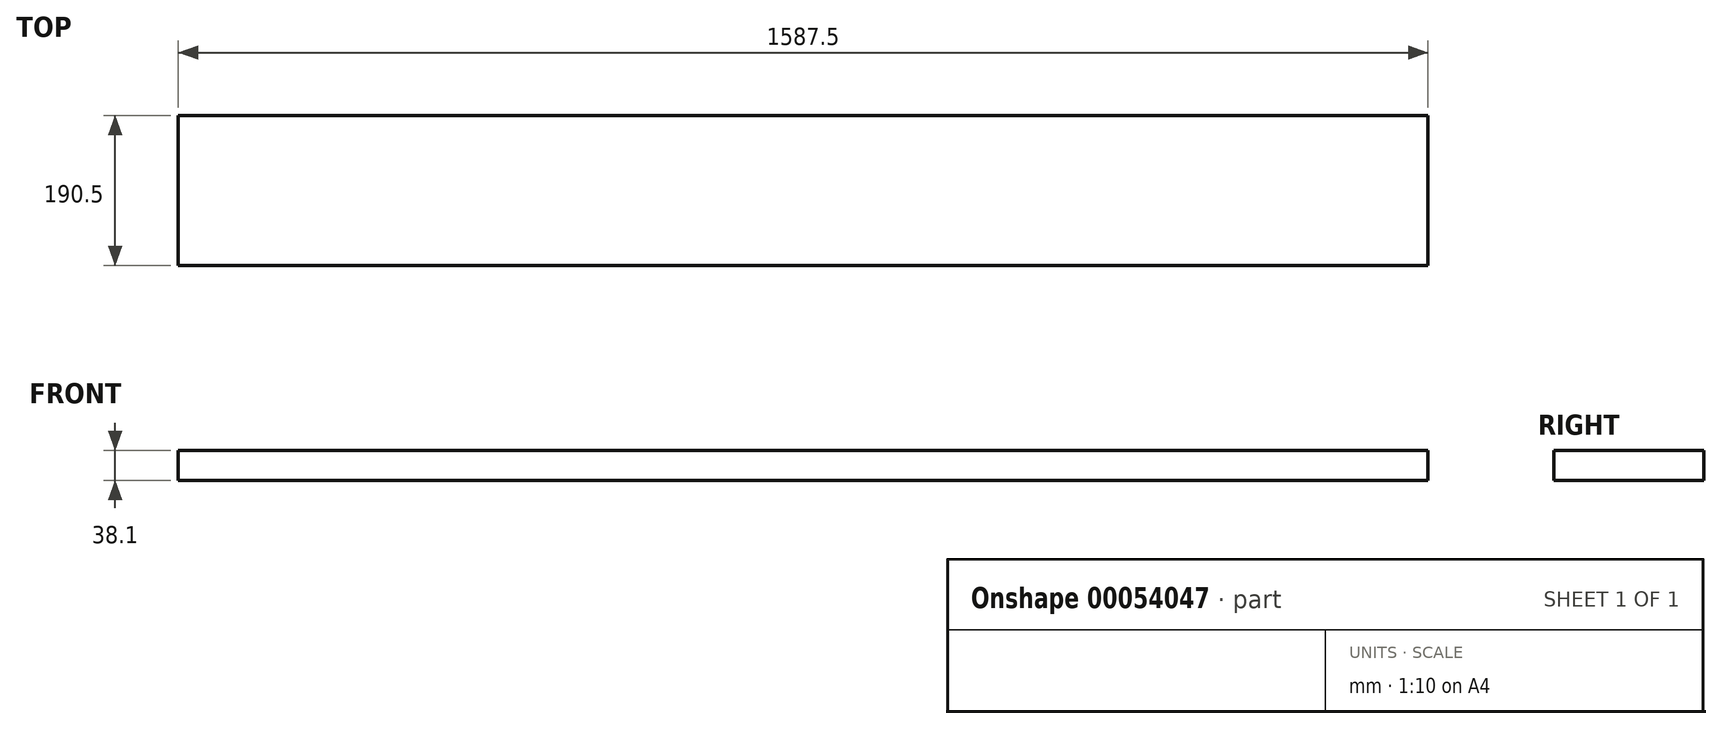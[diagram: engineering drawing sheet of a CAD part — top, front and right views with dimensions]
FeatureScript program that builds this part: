
annotation { "Feature Type Name" : "Feature", "Feature Type Description" : "" }
export const myFeature = defineFeature(function(context is Context, id is Id, definition is map)
    precondition{}
    {
        {
            var Q0;
            Q0=qCreatedBy(makeId("Right.planeOp"),FACE);
            var sketch = newSketch(context, id + "F0", { "sketchPlane" : qUnion([Q0])});
            skLineSegment(sketch, "E0.bottom", {"start": v(0, 0) * mm, "end": v(190.5, 0) * mm});
            skLineSegment(sketch, "E0.top", {"start": v(0, 38.1) * mm, "end": v(190.5, 38.1) * mm});
            skLineSegment(sketch, "E0.left", {"start": v(0, 0) * mm, "end": v(0, 38.1) * mm});
            skLineSegment(sketch, "E0.right", {"start": v(190.5, 0) * mm, "end": v(190.5, 38.1) * mm});
            skSolve(sketch);
        }
        {
            var Q0;
            Q0=makeQuery(id+"F0.imprint","IMPRINT",FACE,{"disambiguationData":[TD([[makeQuery(id+"F0.imprint","IMPRINT",EDGE,{"derivedFrom":sQuery(id+"F0.wireOp",EDGE,"E0.bottom")}),1.0]])]});
            extrude(context, id + "F1", {"entities" : qUnion([Q0]), "depth" : 1587.5 * mm});
        }
    });
